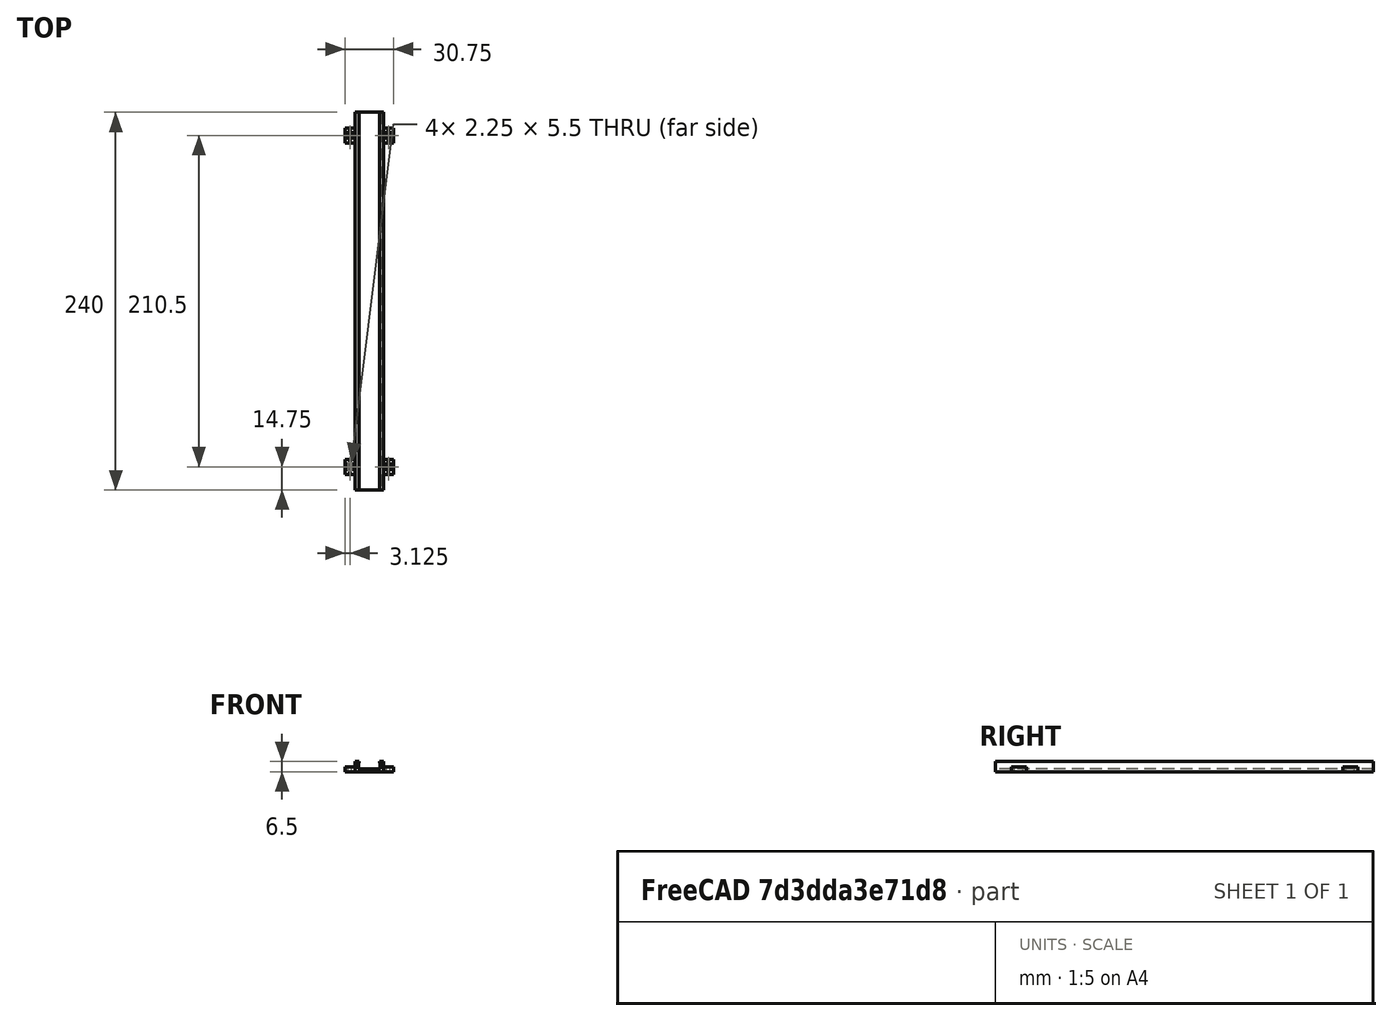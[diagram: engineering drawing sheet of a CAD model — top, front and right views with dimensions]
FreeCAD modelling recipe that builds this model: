
FCSTD DOCUMENT  (FreeCAD 0.19R)
Label: led-strip-mount
License: All rights reserved
LicenseURL: http://en.wikipedia.org/wiki/All_rights_reserved
objects: Sketcher::SketchObject×2, PartDesign::Pad×2, PartDesign::Body×1, Mesh::Feature×1
note: 7 computed .brp shape members not serialized (recipe doc carries the construction recipe); baked Part::Feature solids carry a one-line shape summary decoded from their .brp

FEATURE [Sketcher::SketchObject] Sketch
  FullyConstrained = true
  MapMode = 5
  Placement = pos=(0,0,0) rot=(1,0,0;1.5708rad)
  Support = -> [XZ_Plane]
  sketch-geometry (10):
    g0: LineSegment StartX=0 StartY=0 StartZ=0 EndX=18.25 EndY=0 EndZ=0
    g1: LineSegment StartX=0 StartY=0 StartZ=0 EndX=0 EndY=6.5 EndZ=0
    g2: LineSegment StartX=0 StartY=6.5 StartZ=0 EndX=2.5 EndY=6.5 EndZ=0
    g3: LineSegment StartX=2.5 StartY=6.5 StartZ=0 EndX=2 EndY=2 EndZ=0
    g4: LineSegment StartX=2 StartY=2 StartZ=0 EndX=16.25 EndY=2 EndZ=0
    g5: LineSegment StartX=16.25 StartY=2 StartZ=0 EndX=15.75 EndY=6.5 EndZ=0
    g6: LineSegment StartX=15.75 StartY=6.5 StartZ=0 EndX=18.25 EndY=6.5 EndZ=0
    g7: LineSegment StartX=18.25 StartY=6.5 StartZ=0 EndX=18.25 EndY=0 EndZ=0
    g8: LineSegment StartX=2.5 StartY=6.5 StartZ=0 EndX=15.75 EndY=6.5 EndZ=0
    g9: LineSegment StartX=9.125 StartY=2 StartZ=0 EndX=9.125 EndY=6.5 EndZ=0
  constraints (27):
    c: Coincident(g0,g-1)
    c: PointOnObject(g0,g-1)
    c: Coincident(g1,g0)
    c: Coincident(g2,g1)
    c: Coincident(g3,g2)
    c: Coincident(g4,g3)
    c: Horizontal(g4)
    c: Coincident(g5,g4)
    c: Coincident(g6,g5)
    c: Coincident(g7,g6)
    c: Coincident(g7,g0)
    c: DistanceX(g4,g4) = 14.25
    c: DistanceY(g0,g3) = 2
    c: Horizontal(g2)
    c: Horizontal(g6)
    c: DistanceY(g3,g1) = 4.5
    c: DistanceX(g2,g5) = 13.25
    c: Equal(g2,g6)
    c: Coincident(g8,g2)
    c: Coincident(g8,g5)
    c: Vertical(g9)
    c: Horizontal(g8)
    c: Symmetric(g4,g3,g9)
    c: Symmetric(g2,g5,g9)
    c: Vertical(g1)
    c: Vertical(g7)
    c: DistanceX(g0,g3) = 2
FEATURE [PartDesign::Pad] Pad
  Direction = (1,1,1)
  Length = 240
  Length2 = 100
  Placement = pos=(0,0,0) rot=(1,0,0;1.5708rad)
  Profile = -> Sketch
  Type = 0
FEATURE [Sketcher::SketchObject] Sketch001
  FullyConstrained = true
  MapMode = 5
  Support = -> [XY_Plane]
  sketch-geometry (44):
    g0: LineSegment StartX=0 StartY=0 StartZ=0 EndX=18.25 EndY=0 EndZ=0
    g1: LineSegment StartX=18.25 StartY=0 StartZ=0 EndX=18.25 EndY=-240 EndZ=0
    g2: LineSegment StartX=18.25 StartY=-240 StartZ=0 EndX=0 EndY=-240 EndZ=0
    g3: LineSegment StartX=0 StartY=-240 StartZ=0 EndX=0 EndY=0 EndZ=0
    g4: LineSegment StartX=0 StartY=-10 StartZ=0 EndX=-6.25 EndY=-10 EndZ=0
    g5: LineSegment StartX=-6.25 StartY=-10 StartZ=0 EndX=-6.25 EndY=-19.5 EndZ=0
    g6: LineSegment StartX=-6.25 StartY=-19.5 StartZ=0 EndX=0 EndY=-19.5 EndZ=0
    g7: LineSegment StartX=0 StartY=-19.5 StartZ=0 EndX=0 EndY=-10 EndZ=0
    g8: LineSegment StartX=-4.25 StartY=-12 StartZ=0 EndX=-2 EndY=-12 EndZ=0
    g9: LineSegment StartX=-2 StartY=-12 StartZ=0 EndX=-2 EndY=-17.5 EndZ=0
    g10: LineSegment StartX=-2 StartY=-17.5 StartZ=0 EndX=-4.25 EndY=-17.5 EndZ=0
    g11: LineSegment StartX=-4.25 StartY=-17.5 StartZ=0 EndX=-4.25 EndY=-12 EndZ=0
    g12: LineSegment StartX=-3.125 StartY=-12 StartZ=0 EndX=-3.125 EndY=-10 EndZ=0
    g13: LineSegment StartX=-4.25 StartY=-14.75 StartZ=0 EndX=-6.25 EndY=-14.75 EndZ=0
    g14: LineSegment StartX=18.25 StartY=-10 StartZ=0 EndX=24.5 EndY=-10 EndZ=0
    g15: LineSegment StartX=24.5 StartY=-10 StartZ=0 EndX=24.5 EndY=-19.5 EndZ=0
    g16: LineSegment StartX=24.5 StartY=-19.5 StartZ=0 EndX=18.25 EndY=-19.5 EndZ=0
    g17: LineSegment StartX=18.25 StartY=-19.5 StartZ=0 EndX=18.25 EndY=-10 EndZ=0
    g18: LineSegment StartX=20.25 StartY=-12 StartZ=0 EndX=22.5 EndY=-12 EndZ=0
    g19: LineSegment StartX=22.5 StartY=-12 StartZ=0 EndX=22.5 EndY=-17.5 EndZ=0
    g20: LineSegment StartX=22.5 StartY=-17.5 StartZ=0 EndX=20.25 EndY=-17.5 EndZ=0
    g21: LineSegment StartX=20.25 StartY=-17.5 StartZ=0 EndX=20.25 EndY=-12 EndZ=0
    g22: LineSegment StartX=-6.25 StartY=-220.5 StartZ=0 EndX=0 EndY=-220.5 EndZ=0
    g23: LineSegment StartX=0 StartY=-220.5 StartZ=0 EndX=0 EndY=-230 EndZ=0
    g24: LineSegment StartX=0 StartY=-230 StartZ=0 EndX=-6.25 EndY=-230 EndZ=0
    g25: LineSegment StartX=-6.25 StartY=-230 StartZ=0 EndX=-6.25 EndY=-220.5 EndZ=0
    g26: LineSegment StartX=-4.25 StartY=-222.5 StartZ=0 EndX=-2 EndY=-222.5 EndZ=0
    g27: LineSegment StartX=-2 StartY=-222.5 StartZ=0 EndX=-2 EndY=-228 EndZ=0
    g28: LineSegment StartX=-2 StartY=-228 StartZ=0 EndX=-4.25 EndY=-228 EndZ=0
    g29: LineSegment StartX=-4.25 StartY=-228 StartZ=0 EndX=-4.25 EndY=-222.5 EndZ=0
    g30: LineSegment StartX=18.25 StartY=-220.5 StartZ=0 EndX=24.5 EndY=-220.5 EndZ=0
    g31: LineSegment StartX=24.5 StartY=-220.5 StartZ=0 EndX=24.5 EndY=-230 EndZ=0
    g32: LineSegment StartX=24.5 StartY=-230 StartZ=0 EndX=18.25 EndY=-230 EndZ=0
    g33: LineSegment StartX=18.25 StartY=-230 StartZ=0 EndX=18.25 EndY=-220.5 EndZ=0
    g34: LineSegment StartX=20.25 StartY=-222.5 StartZ=0 EndX=22.5 EndY=-222.5 EndZ=0
    g35: LineSegment StartX=22.5 StartY=-222.5 StartZ=0 EndX=22.5 EndY=-228 EndZ=0
    g36: LineSegment StartX=22.5 StartY=-228 StartZ=0 EndX=20.25 EndY=-228 EndZ=0
    g37: LineSegment StartX=20.25 StartY=-228 StartZ=0 EndX=20.25 EndY=-222.5 EndZ=0
    g38: LineSegment StartX=21.375 StartY=-12 StartZ=0 EndX=21.375 EndY=-10 EndZ=0
    g39: LineSegment StartX=22.5 StartY=-14.75 StartZ=0 EndX=24.5 EndY=-14.75 EndZ=0
    g40: LineSegment StartX=-4.25 StartY=-225.25 StartZ=0 EndX=-6.25 EndY=-225.25 EndZ=0
    g41: LineSegment StartX=22.5 StartY=-225.25 StartZ=0 EndX=24.5 EndY=-225.25 EndZ=0
    g42: LineSegment StartX=-3.125 StartY=-230 StartZ=0 EndX=-3.125 EndY=-228 EndZ=0
    g43: LineSegment StartX=21.375 StartY=-230 StartZ=0 EndX=21.375 EndY=-228 EndZ=0
  constraints (123):
    c: Coincident(g0,g1)
    c: Coincident(g1,g2)
    c: Coincident(g2,g3)
    c: Coincident(g3,g0)
    c: Horizontal(g0)
    c: Horizontal(g2)
    c: Vertical(g1)
    c: Vertical(g3)
    c: Coincident(g0,g-1)
    c: DistanceY(g1,g1) = 240
    c: DistanceX(g0,g0) = 18.25
    c: Coincident(g4,g5)
    c: Coincident(g5,g6)
    c: Coincident(g6,g7)
    c: Coincident(g7,g4)
    c: Horizontal(g4)
    c: Horizontal(g6)
    c: Vertical(g5)
    c: Vertical(g7)
    c: PointOnObject(g4,g3)
    c: Coincident(g8,g9)
    c: Coincident(g9,g10)
    c: Coincident(g10,g11)
    c: Coincident(g11,g8)
    c: Horizontal(g8)
    c: Horizontal(g10)
    c: Vertical(g9)
    c: Vertical(g11)
    c: DistanceX(g10,g10) = 2.25
    c: DistanceY(g9,g9) = 5.5
    c: Vertical(g12)
    c: Horizontal(g13)
    c: Symmetric(g4,g4,g12)
    c: Symmetric(g8,g8,g12)
    c: Symmetric(g8,g10,g13)
    c: Symmetric(g4,g5,g13)
    c: DistanceX(g4,g8) = 2
    c: DistanceY(g8,g4) = 2
    c: DistanceY(g4,g-1) = 10
    c: Coincident(g14,g15)
    c: Coincident(g15,g16)
    c: Coincident(g16,g17)
    c: Coincident(g17,g14)
    c: Horizontal(g14)
    c: Horizontal(g16)
    c: Vertical(g15)
    c: Vertical(g17)
    c: PointOnObject(g14,g1)
    c: Coincident(g18,g19)
    c: Coincident(g19,g20)
    c: Coincident(g20,g21)
    c: Coincident(g21,g18)
    c: Horizontal(g18)
    c: Horizontal(g20)
    c: Vertical(g19)
    c: Vertical(g21)
    c: Coincident(g22,g23)
    c: Coincident(g23,g24)
    c: Coincident(g24,g25)
    c: Coincident(g25,g22)
    c: Horizontal(g22)
    c: Horizontal(g24)
    c: Vertical(g23)
    c: Vertical(g25)
    c: PointOnObject(g23,g3)
    c: Coincident(g26,g27)
    c: Coincident(g27,g28)
    c: Coincident(g28,g29)
    c: Coincident(g29,g26)
    c: Horizontal(g26)
    c: Horizontal(g28)
    c: Vertical(g27)
    c: Vertical(g29)
    c: Coincident(g30,g31)
    c: Coincident(g31,g32)
    c: Coincident(g32,g33)
    c: Coincident(g33,g30)
    c: Horizontal(g30)
    c: Horizontal(g32)
    c: Vertical(g31)
    c: Vertical(g33)
    c: PointOnObject(g30,g1)
    c: Coincident(g34,g35)
    c: Coincident(g35,g36)
    c: Coincident(g36,g37)
    c: Coincident(g37,g34)
    c: Horizontal(g34)
    c: Horizontal(g36)
    c: Vertical(g35)
    c: Vertical(g37)
    c: Vertical(g38)
    c: Horizontal(g39)
    c: Horizontal(g40)
    c: Horizontal(g41)
    c: DistanceY(g14,g0) = 10
    c: Symmetric(g14,g14,g38)
    c: Symmetric(g15,g14,g39)
    c: Symmetric(g18,g18,g38)
    c: Symmetric(g19,g18,g39)
    c: Symmetric(g26,g28,g40)
    c: Symmetric(g24,g22,g40)
    c: DistanceY(g2,g23) = 10
    c: Symmetric(g31,g30,g41)
    c: Symmetric(g35,g34,g41)
    c: DistanceY(g1,g32) = 10
    c: Equal(g4,g14)
    c: Equal(g14,g22)
    c: Equal(g22,g30)
    c: Equal(g5,g15)
    c: Equal(g15,g25)
    c: Equal(g25,g31)
    c: Equal(g10,g20)
    c: Equal(g20,g26)
    c: Equal(g26,g34)
    c: Equal(g9,g21)
    c: Equal(g21,g27)
    c: Equal(g27,g37)
    c: Vertical(g42)
    c: Vertical(g43)
    c: Symmetric(g31,g32,g43)
    c: Symmetric(g35,g36,g43)
    c: Symmetric(g23,g24,g42)
    c: Symmetric(g27,g28,g42)
FEATURE [PartDesign::Pad] Pad001
  BaseFeature = -> Pad
  Direction = (1,1,1)
  Length = 3.25
  Length2 = 100
  Placement = pos=(0,0,0) rot=(1,0,0;1.5708rad)
  Profile = -> Sketch001
  Type = 0
FEATURE [PartDesign::Body] Body
  Group = -> [Sketch,Pad,Sketch001,Pad001]
  Origin = -> Origin
  Tip = -> Pad001
FEATURE [Mesh::Feature] Mesh  label="Body (Meshed)"
